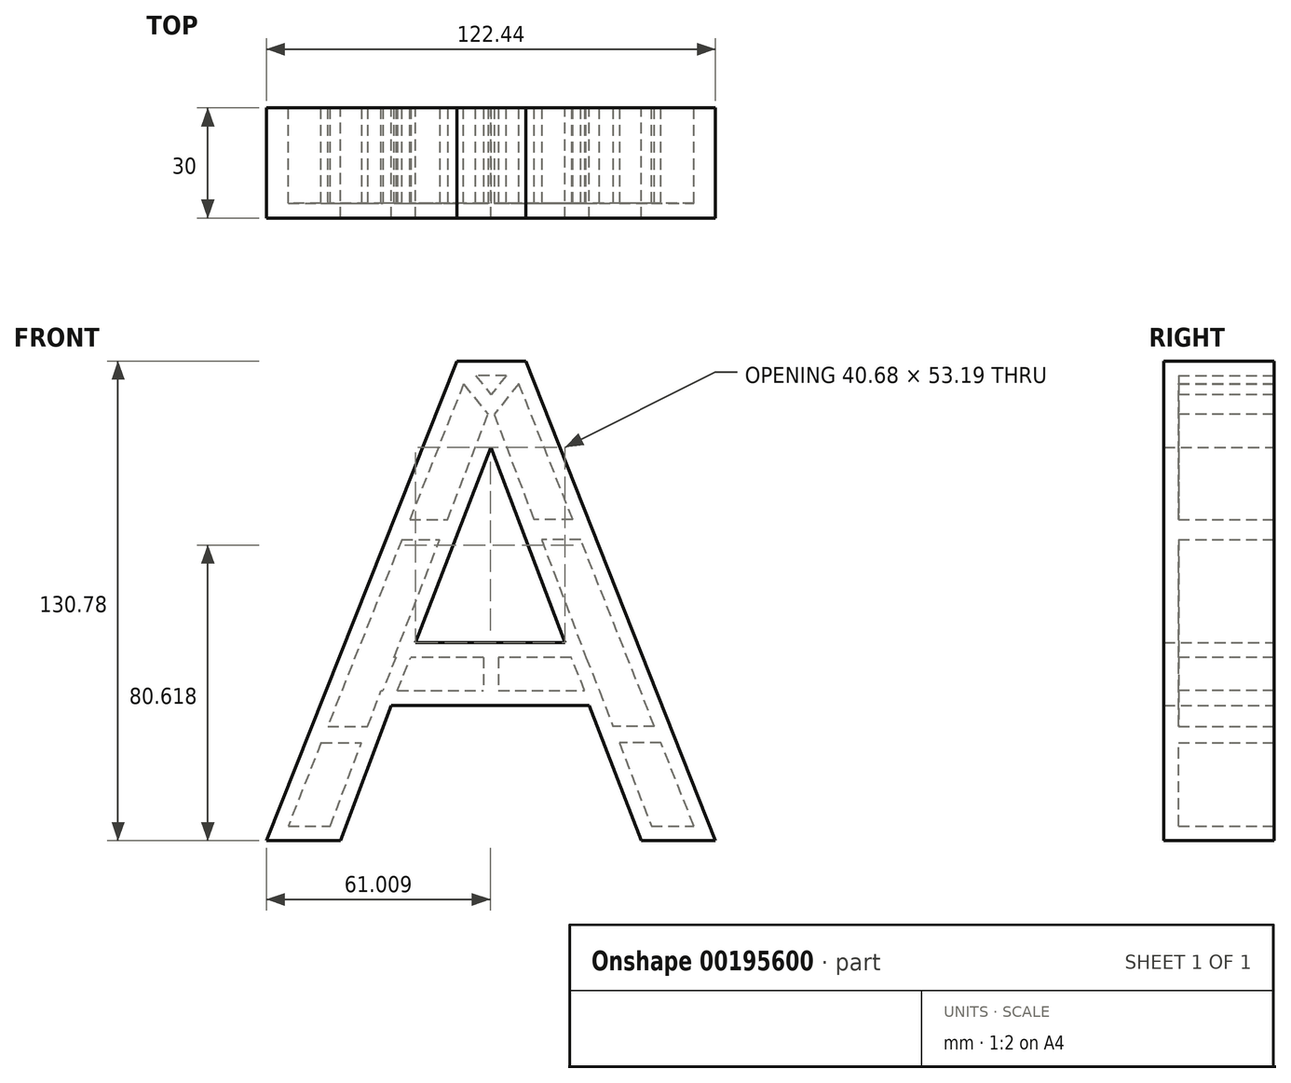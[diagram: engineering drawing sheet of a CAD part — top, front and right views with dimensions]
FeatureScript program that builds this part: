
annotation { "Feature Type Name" : "Feature", "Feature Type Description" : "" }
export const myFeature = defineFeature(function(context is Context, id is Id, definition is map)
    precondition{}
    {
        {
            var Q0;
            Q0=qCreatedBy(makeId("Front.planeOp"),FACE);
            var sketch = newSketch(context, id + "F0", { "sketchPlane" : qUnion([Q0])});
            skLineSegment(sketch, "E0", {"start": v(9.49, 65.4) * mm, "end": v(-9.28, 65.4) * mm});
            skLineSegment(sketch, "E1", {"start": v(-9.28, 65.4) * mm, "end": v(-61.22, -65.4) * mm});
            skLineSegment(sketch, "E2", {"start": v(-61.22, -65.4) * mm, "end": v(-41.08, -65.4) * mm});
            skLineSegment(sketch, "E3", {"start": v(-41.08, -65.4) * mm, "end": v(-27.22, -28.47) * mm});
            skLineSegment(sketch, "E4", {"start": v(-27.22, -28.47) * mm, "end": v(26.8, -28.47) * mm});
            skLineSegment(sketch, "E5", {"start": v(26.8, -28.47) * mm, "end": v(40.99, -65.4) * mm});
            skLineSegment(sketch, "E6", {"start": v(40.99, -65.4) * mm, "end": v(61.22, -65.4) * mm});
            skLineSegment(sketch, "E7", {"start": v(61.22, -65.4) * mm, "end": v(9.49, 65.4) * mm});
            skLineSegment(sketch, "E8", {"start": v(-20.55, -11.37) * mm, "end": v(0, 41.83) * mm});
            skLineSegment(sketch, "E9", {"start": v(0, 41.83) * mm, "end": v(20.13, -11.37) * mm});
            skLineSegment(sketch, "E10", {"start": v(20.13, -11.37) * mm, "end": v(-20.55, -11.37) * mm});
            skSolve(sketch);
        }
        {
            var Q0;
            Q0 = qSketchRegion(id + "F0", true);
            extrude(context, id + "F1", {"entities" : qUnion([Q0]), "depth" : 30 * mm});
        }
        {
            var Q0;
            Q0=makeQuery(id+"F1.opExtrude","CAP_FACE",FACE,{"disambiguationData":[OSD([sQuery(id+"F0.wireOp",EDGE,"E0"),sQuery(id+"F0.wireOp",EDGE,"E1"),sQuery(id+"F0.wireOp",EDGE,"E2"),sQuery(id+"F0.wireOp",EDGE,"E3"),sQuery(id+"F0.wireOp",EDGE,"E4"),sQuery(id+"F0.wireOp",EDGE,"E5"),sQuery(id+"F0.wireOp",EDGE,"E6"),sQuery(id+"F0.wireOp",EDGE,"E7"),sQuery(id+"F0.wireOp",EDGE,"E8"),sQuery(id+"F0.wireOp",EDGE,"E9"),sQuery(id+"F0.wireOp",EDGE,"E10")])],"isStart":true});
            shell(context, id + "F2", {"entities" : qUnion([Q0]), "thickness" : 4 * mm});
        }
        {
            var Q0;
            {var subQ0=sQuery(id+"F0.wireOp",EDGE,"E10");var subQ1=sQuery(id+"F0.wireOp",EDGE,"E9");var subQ2=sQuery(id+"F0.wireOp",EDGE,"E8");var subQ3=sQuery(id+"F0.wireOp",EDGE,"E7");var subQ4=sQuery(id+"F0.wireOp",EDGE,"E6");var subQ5=sQuery(id+"F0.wireOp",EDGE,"E5");var subQ6=sQuery(id+"F0.wireOp",EDGE,"E4");var subQ7=sQuery(id+"F0.wireOp",EDGE,"E3");var subQ8=sQuery(id+"F0.wireOp",EDGE,"E2");var subQ9=sQuery(id+"F0.wireOp",EDGE,"E1");var subQ10=sQuery(id+"F0.wireOp",EDGE,"E0");Q0=makeQuery(id+"F2.opShell","OFFSET_FACE",FACE,{"disambiguationData":[OSD([subQ10,subQ9,subQ8,subQ7,subQ6,subQ5,subQ4,subQ3,subQ2,subQ1,subQ0]),TDD([makeQuery(id+"F1.opExtrude","CAP_FACE",FACE,{"disambiguationData":[OSD([subQ10,subQ9,subQ8,subQ7,subQ6,subQ5,subQ4,subQ3,subQ2,subQ1,subQ0])],"isStart":false})])]});}
            var sketch = newSketch(context, id + "F3", { "sketchPlane" : qUnion([Q0])});
            skLineSegment(sketch, "E11", {"start": v(-25.92, -15.37) * mm, "end": v(-29.55, -24.47) * mm});
            skLineSegment(sketch, "E12", {"start": v(-29.55, -24.47) * mm, "end": v(-25.55, -24.47) * mm});
            skLineSegment(sketch, "E13", {"start": v(-25.55, -24.47) * mm, "end": v(-21.92, -15.37) * mm});
            skLineSegment(sketch, "E14", {"start": v(-25.92, -15.37) * mm, "end": v(-21.92, -15.37) * mm});
            skLineSegment(sketch, "E15.bottom", {"start": v(-2, -15.37) * mm, "end": v(2, -15.37) * mm});
            skLineSegment(sketch, "E15.top", {"start": v(-2, -24.47) * mm, "end": v(2, -24.47) * mm});
            skLineSegment(sketch, "E15.left", {"start": v(-2, -15.37) * mm, "end": v(-2, -24.47) * mm});
            skLineSegment(sketch, "E15.right", {"start": v(2, -15.37) * mm, "end": v(2, -24.47) * mm});
            skLineSegment(sketch, "E16.bottom", {"start": v(-47.53, -34.2) * mm, "end": v(-32.8, -34.2) * mm});
            skLineSegment(sketch, "E16.top", {"start": v(-47.53, -38.7) * mm, "end": v(-32.8, -38.7) * mm});
            skLineSegment(sketch, "E16.left", {"start": v(-47.53, -34.2) * mm, "end": v(-47.53, -38.7) * mm});
            skLineSegment(sketch, "E16.right", {"start": v(-32.8, -34.2) * mm, "end": v(-32.8, -38.7) * mm});
            skLineSegment(sketch, "E17.bottom", {"start": v(-25.57, 22.16) * mm, "end": v(-10.46, 22.16) * mm});
            skLineSegment(sketch, "E17.top", {"start": v(-25.57, 16.73) * mm, "end": v(-10.46, 16.73) * mm});
            skLineSegment(sketch, "E17.left", {"start": v(-25.57, 22.16) * mm, "end": v(-25.57, 16.73) * mm});
            skLineSegment(sketch, "E17.right", {"start": v(-10.46, 22.16) * mm, "end": v(-10.46, 16.73) * mm});
            skLineSegment(sketch, "E18.0", {"start": v(-8.33, 60.14) * mm, "end": v(-1.6, 51.77) * mm});
            skLineSegment(sketch, "E19.0", {"start": v(-5.21, 62.65) * mm, "end": v(0, 56.17) * mm});
            skLineSegment(sketch, "E20", {"start": v(-1.6, 51.77) * mm, "end": v(0, 49.79) * mm});
            skLineSegment(sketch, "E21", {"start": v(-8.33, 60.14) * mm, "end": v(-5.21, 62.65) * mm});
            skLineSegment(sketch, "E22", {"start": v(0, 34.28) * mm, "end": v(0, 18.14) * mm, "construction": true});
            skLineSegment(sketch, "E23.MirrorCS", {"start": v(1.6, 51.77) * mm, "end": v(0, 49.79) * mm});
            skLineSegment(sketch, "E24.MirrorCS", {"start": v(8.33, 60.14) * mm, "end": v(5.21, 62.65) * mm});
            skLineSegment(sketch, "E25.MirrorCS", {"start": v(5.21, 62.65) * mm, "end": v(0, 56.17) * mm});
            skLineSegment(sketch, "E26.MirrorCS", {"start": v(8.33, 60.14) * mm, "end": v(1.6, 51.77) * mm});
            skLineSegment(sketch, "E27.MirrorCS", {"start": v(10.46, 22.16) * mm, "end": v(10.46, 16.73) * mm});
            skLineSegment(sketch, "E28.MirrorCS", {"start": v(25.57, 22.16) * mm, "end": v(25.57, 16.73) * mm});
            skLineSegment(sketch, "E29.MirrorCS", {"start": v(25.57, 16.73) * mm, "end": v(10.46, 16.73) * mm});
            skLineSegment(sketch, "E30.MirrorCS", {"start": v(25.57, 22.16) * mm, "end": v(10.46, 22.16) * mm});
            skLineSegment(sketch, "E31.MirrorCS", {"start": v(32.8, -34.2) * mm, "end": v(32.8, -38.7) * mm});
            skLineSegment(sketch, "E32.MirrorCS", {"start": v(47.53, -34.2) * mm, "end": v(47.53, -38.7) * mm});
            skLineSegment(sketch, "E33.MirrorCS", {"start": v(29.55, -24.47) * mm, "end": v(25.55, -24.47) * mm});
            skLineSegment(sketch, "E34.MirrorCS", {"start": v(25.92, -15.37) * mm, "end": v(21.92, -15.37) * mm});
            skLineSegment(sketch, "E35.MirrorCS", {"start": v(47.53, -34.2) * mm, "end": v(32.8, -34.2) * mm});
            skLineSegment(sketch, "E36.MirrorCS", {"start": v(47.53, -38.7) * mm, "end": v(32.8, -38.7) * mm});
            skLineSegment(sketch, "E37.MirrorCS", {"start": v(25.55, -24.47) * mm, "end": v(21.92, -15.37) * mm});
            skLineSegment(sketch, "E38.MirrorCS", {"start": v(25.92, -15.37) * mm, "end": v(29.55, -24.47) * mm});
            skPoint(sketch, "E39.orphan", {"position": v(-1.52, 54.28) * mm});
            skPoint(sketch, "E40.orphan", {"position": v(1.52, 54.28) * mm});
            skSolve(sketch);
        }
        {
            var Q0;
            Q0 = qSketchRegion(id + "F3", true);
            extrude(context, id + "F4", {"entities" : qUnion([Q0]), "operationType" : NewBodyOperationType.ADD, "depth" : 26 * mm});
        }
    });
